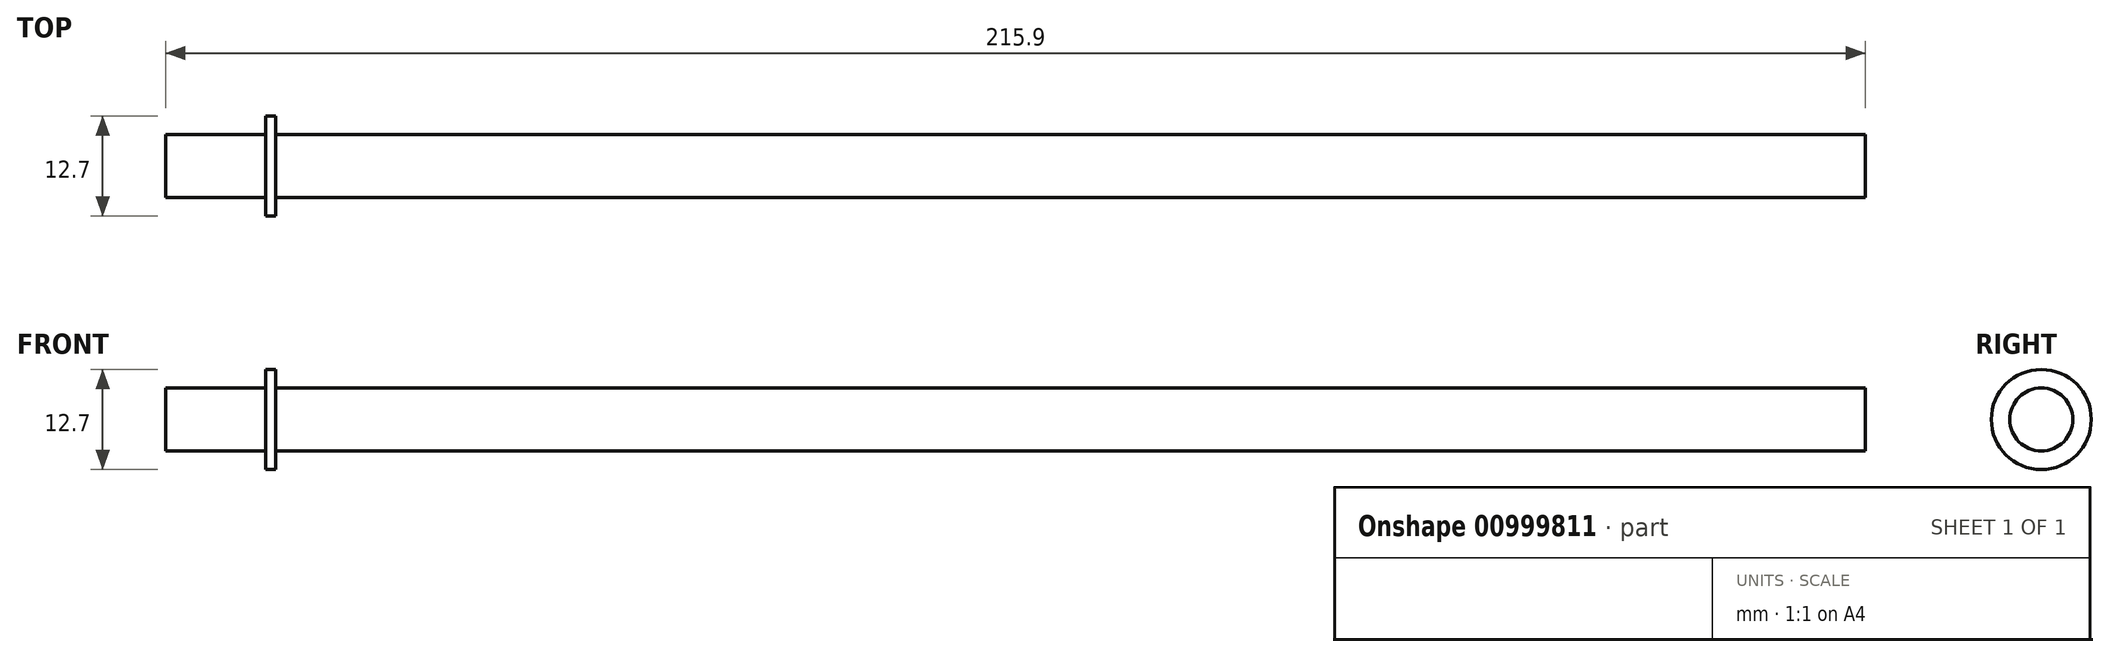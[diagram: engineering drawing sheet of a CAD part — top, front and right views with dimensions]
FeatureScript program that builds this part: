
annotation { "Feature Type Name" : "Feature", "Feature Type Description" : "" }
export const myFeature = defineFeature(function(context is Context, id is Id, definition is map)
    precondition{}
    {
        {
            var Q0;
            Q0=qCreatedBy(makeId("Right.planeOp"),FACE);
            var sketch = newSketch(context, id + "F0", { "sketchPlane" : qUnion([Q0])});
            skCircle(sketch, "E0", {"center": v(0, 0) * mm, "radius": 4 * mm});
            skSolve(sketch);
        }
        {
            var Q0;
            Q0=makeQuery(id+"F0.imprint","IMPRINT",FACE,{"disambiguationData":[TD([[makeQuery(id+"F0.imprint","IMPRINT",EDGE,{"derivedFrom":sQuery(id+"F0.wireOp",EDGE,"E0")}),1.0]])]});
            extrude(context, id + "F1", {"entities" : qUnion([Q0]), "depth" : 203.2 * mm, "offsetDistance" : 25.4 * mm});
        }
        {
            var Q0;
            Q0=qCreatedBy(makeId("Right.planeOp"),FACE);
            var sketch = newSketch(context, id + "F2", { "sketchPlane" : qUnion([Q0])});
            skCircle(sketch, "E1", {"center": v(0, 0) * mm, "radius": 6.35 * mm});
            skSolve(sketch);
        }
        {
            var Q0;
            Q0=makeQuery(id+"F2.imprint","IMPRINT",FACE,{"disambiguationData":[TD([[makeQuery(id+"F2.imprint","IMPRINT",EDGE,{"derivedFrom":sQuery(id+"F2.wireOp",EDGE,"E1")}),1.0]])]});
            extrude(context, id + "F3", {"entities" : qUnion([Q0]), "operationType" : NewBodyOperationType.ADD, "depth" : 1.27 * mm, "offsetDistance" : 25.4 * mm});
        }
        {
            var Q0;
            Q0=qCreatedBy(makeId("Right.planeOp"),FACE);
            var sketch = newSketch(context, id + "F4", { "sketchPlane" : qUnion([Q0])});
            skCircle(sketch, "E2", {"center": v(0, 0) * mm, "radius": 4 * mm});
            skSolve(sketch);
        }
        {
            var Q0;
            Q0=makeQuery(id+"F4.imprint","IMPRINT",FACE,{"disambiguationData":[TD([[makeQuery(id+"F4.imprint","IMPRINT",EDGE,{"derivedFrom":sQuery(id+"F4.wireOp",EDGE,"E2")}),1.0]])]});
            extrude(context, id + "F5", {"entities" : qUnion([Q0]), "operationType" : NewBodyOperationType.ADD, "oppositeDirection" : true, "depth" : 12.7 * mm, "offsetDistance" : 25.4 * mm});
        }
    });
